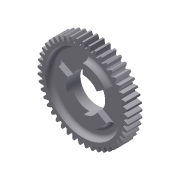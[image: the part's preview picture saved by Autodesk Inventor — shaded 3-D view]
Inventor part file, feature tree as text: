
AUTODESK INVENTOR PART (.ipt)
format: ipt  version: 2011 (Build 150239000, 239)  size: 401,920 bytes
history: native  units: mm (DEFAULTED — no unit token found)
features: sketch x5, other x4, extrude x3, plane x3, revolve x1, pattern_circular x1, fillet x1, projected_geometry x1
ambient origin geometry x8: Origin, YZ Plane, XZ Plane, XY Plane, X Axis, Y Axis, Z Axis, Center Point
bodies: Solid1 (feature_tree)
feature tree (19):
  other  "Gear 45T dog shift"
  extrude  "Extrusion1"  Depth=9.525mm TaperAngle=0.0deg
  plane  "Work Plane1"
  plane  "Work Plane2"
  plane  "Work Plane3"
  other  "Spur Gear"
  extrude  "Extrusion4"  Depth=76.2mm TaperAngle=0.0deg
  revolve  "Revolution2"  [1 undecoded]
  extrude  "Extrusion6"  TaperAngle=0.0deg  [1 undecoded]
  pattern_circular  "Circular Pattern2"  [2 undecoded]
  fillet  "Fillet1"  Radius=25.4mm
  sketch  "Sketch1"  dims[d0=59.69mm d1=9.525mm d2=0.0mm]
  sketch  "Sketch2"  dims[d3=57.15mm d4=76.2mm d5=0.0mm]
  other  "Srf1"
  sketch  "Sketch6"  dims[d6=0.0mm d7=0.698132mm d9=0.0mm]
  sketch  "Sketch8"  dims[d14=0.0mm d15=142.875mm d16=0.0mm]
  sketch  "Sketch9"  dims[d17=0.0mm d18=0.0mm d19=142.875mm d31=22.225mm d32=25.4mm d33=0.0mm d42=5.08mm d43=3.6576mm d44=17.78mm d45=90.0deg d46=11.170107mm d47=3.6576mm d48=0.0mm d49=30.0mm d50=360.0deg d52=2.54mm]
  other  "Pitch Diameter"
  projected_geometry  "Project Cut Edges2"
note: 4 required parameter values undecoded (feature->parameter linkage not recoverable at this tier; creation-order binding heuristic only, values carry confidence <= 0.55)